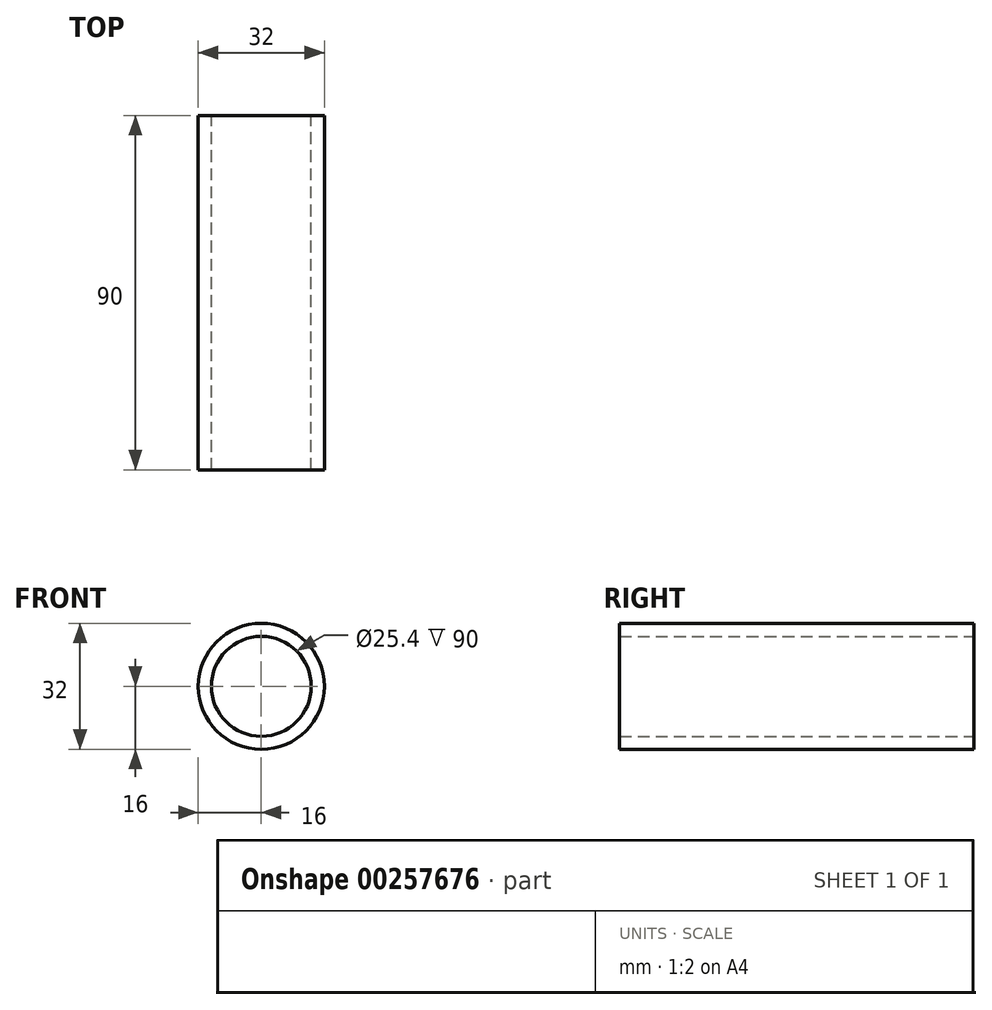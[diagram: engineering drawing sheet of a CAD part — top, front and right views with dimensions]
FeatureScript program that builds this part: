
annotation { "Feature Type Name" : "Feature", "Feature Type Description" : "" }
export const myFeature = defineFeature(function(context is Context, id is Id, definition is map)
    precondition{}
    {
        {
            var Q0;
            Q0=qCreatedBy(makeId("Front.planeOp"),FACE);
            var sketch = newSketch(context, id + "F0", { "sketchPlane" : qUnion([Q0])});
            skCircle(sketch, "E0", {"center": v(0, 0) * mm, "radius": 16 * mm});
            skCircle(sketch, "E1", {"center": v(0, 0) * mm, "radius": 12.7 * mm});
            skSolve(sketch);
        }
        {
            var Q0;
            Q0=makeQuery(id+"F0.imprint","IMPRINT",FACE,{"disambiguationData":[TD([[makeQuery(id+"F0.imprint","IMPRINT",EDGE,{"derivedFrom":sQuery(id+"F0.wireOp",EDGE,"E0")}),1.0]])]});
            extrude(context, id + "F1", {"entities" : qUnion([Q0]), "depth" : 90 * mm});
        }
    });
